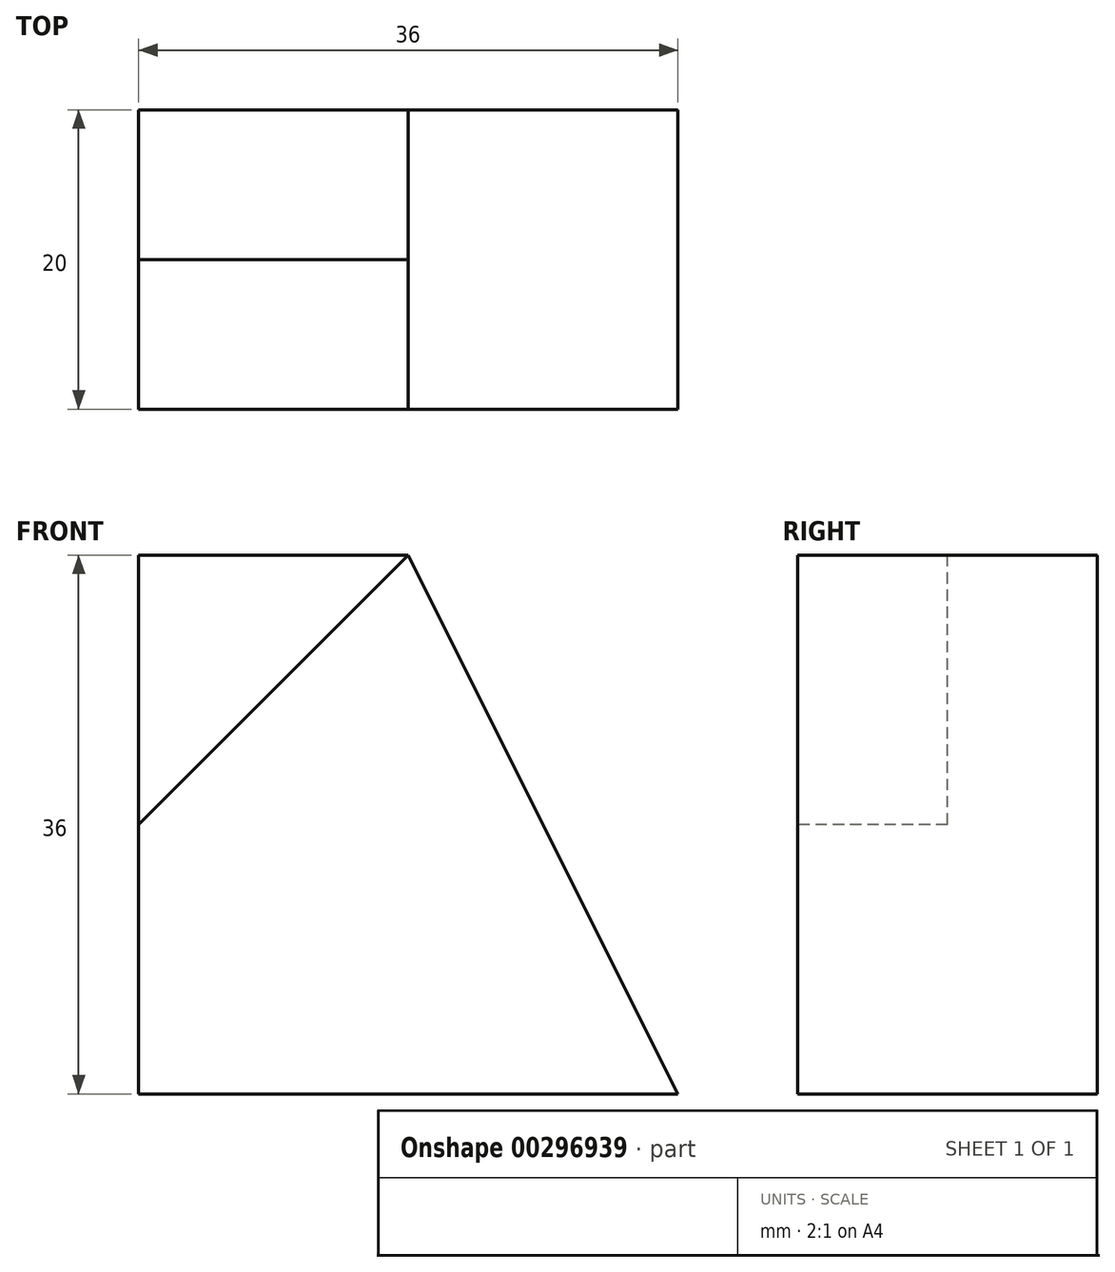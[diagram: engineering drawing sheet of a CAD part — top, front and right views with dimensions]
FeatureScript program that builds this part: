
annotation { "Feature Type Name" : "Feature", "Feature Type Description" : "" }
export const myFeature = defineFeature(function(context is Context, id is Id, definition is map)
    precondition{}
    {
        {
            var Q0;
            Q0=qCreatedBy(makeId("Front.planeOp"),FACE);
            var sketch = newSketch(context, id + "F0", { "sketchPlane" : qUnion([Q0])});
            skLineSegment(sketch, "E0.bottom", {"start": v(0, 0) * mm, "end": v(36, 0) * mm});
            skLineSegment(sketch, "E0.top", {"start": v(0, 36) * mm, "end": v(36, 36) * mm});
            skLineSegment(sketch, "E0.left", {"start": v(0, 0) * mm, "end": v(0, 36) * mm});
            skLineSegment(sketch, "E0.right", {"start": v(36, 0) * mm, "end": v(36, 36) * mm});
            skLineSegment(sketch, "E1", {"start": v(18, 36) * mm, "end": v(36, 0) * mm});
            skLineSegment(sketch, "E2", {"start": v(18, 36) * mm, "end": v(0, 18) * mm});
            skSolve(sketch);
        }
        {
            var Q0;
            Q0=makeQuery(id+"F0.imprint","IMPRINT",FACE,{"disambiguationData":[TD([[makeQuery(id+"F0.imprint","IMPRINT",EDGE,{"derivedFrom":sQuery(id+"F0.wireOp",EDGE,"E0.bottom")}),1.0]])]});
            var Q1;
            {var subQ3=sQuery(id+"F0.wireOp",EDGE,"E2");Q1=makeQuery(id+"F0.imprint","IMPRINT",FACE,{"disambiguationData":[TD([[makeQuery(id+"F0.imprint","IMPRINT",EDGE,{"derivedFrom":subQ3}),-1.0]])]});}
            extrude(context, id + "F1", {"entities" : qUnion([Q0, Q1]), "oppositeDirection" : true, "depth" : 20 * mm});
        }
        {
            var Q0;
            {var subQ3=sQuery(id+"F0.wireOp",EDGE,"E2");Q0=makeQuery(id+"F0.imprint","IMPRINT",FACE,{"disambiguationData":[TD([[makeQuery(id+"F0.imprint","IMPRINT",EDGE,{"derivedFrom":subQ3}),-1.0]])]});}
            extrude(context, id + "F2", {"entities" : qUnion([Q0]), "operationType" : NewBodyOperationType.REMOVE, "oppositeDirection" : true, "depth" : 10 * mm});
        }
    });
